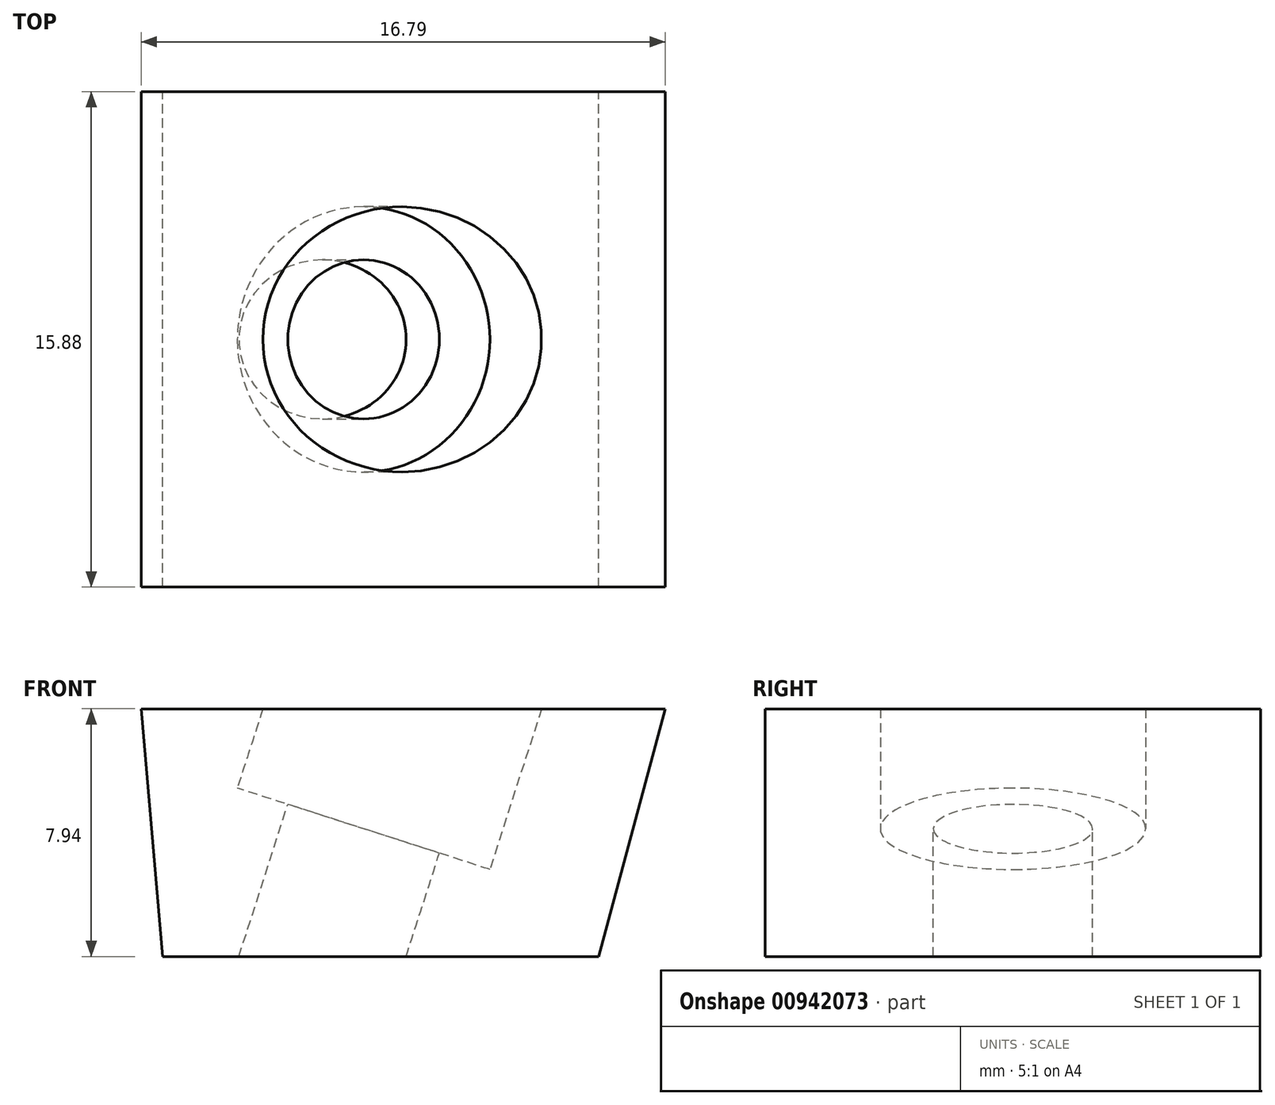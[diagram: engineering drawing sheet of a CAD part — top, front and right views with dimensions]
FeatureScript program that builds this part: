
annotation { "Feature Type Name" : "Feature", "Feature Type Description" : "" }
export const myFeature = defineFeature(function(context is Context, id is Id, definition is map)
    precondition{}
    {
        {
            var Q0;
            Q0=qCreatedBy(makeId("Front.planeOp"),FACE);
            var sketch = newSketch(context, id + "F0", { "sketchPlane" : qUnion([Q0])});
            skLineSegment(sketch, "E0", {"start": v(0, 0) * mm, "end": v(2.13, 7.94) * mm});
            skLineSegment(sketch, "E1", {"start": v(2.13, 7.94) * mm, "end": v(-14.66, 7.94) * mm});
            skLineSegment(sketch, "E2", {"start": v(-14.66, 7.94) * mm, "end": v(-13.97, 0) * mm});
            skLineSegment(sketch, "E3", {"start": v(-13.97, 0) * mm, "end": v(0, 0) * mm});
            skSolve(sketch);
        }
        {
            var Q0;
            Q0=makeQuery(id+"F0.imprint","IMPRINT",FACE,{"disambiguationData":[TD([[makeQuery(id+"F0.imprint","IMPRINT",EDGE,{"derivedFrom":sQuery(id+"F0.wireOp",EDGE,"E0")}),1.0]])]});
            extrude(context, id + "F1", {"entities" : qUnion([Q0]), "depth" : 7.94 * mm, "offsetDistance" : 25.4 * mm, "hasSecondDirection" : true, "secondDirectionOppositeDirection" : true, "secondDirectionDepth" : 7.94 * mm});
        }
        {
            var Q0;
            Q0=qCreatedBy(makeId("Front.planeOp"),FACE);
            var sketch = newSketch(context, id + "F2", { "sketchPlane" : qUnion([Q0])});
            skLineSegment(sketch, "E4", {"start": v(0, 0) * mm, "end": v(-7.98, 2.57) * mm});
            skLineSegment(sketch, "E5", {"start": v(-7.98, 2.57) * mm, "end": v(-1.12, 23.86) * mm});
            skLineSegment(sketch, "E6", {"start": v(-1.12, 23.86) * mm, "end": v(-10.56, -5.44) * mm});
            skSolve(sketch);
        }
        {
            var Q0;
            Q0=sQuery(id+"F2.wireOp",EDGE,"E4");
            cPlane(context, id + "F3", {"entities" : qUnion([Q0]), "cplaneType" : CPlaneType.LINE_ANGLE, "offset" : 25.4 * mm, "angle" : 90 * degree, "width" : 152.4 * mm, "height" : 152.4 * mm});
        }
        {
            var Q0;
            Q0=qCreatedBy(id+"F3.planeOp",FACE);
            var sketch = newSketch(context, id + "F4", { "sketchPlane" : qUnion([Q0])});
            skCircle(sketch, "E7", {"center": v(-8.43, 0) * mm, "radius": 2.55 * mm});
            skCircle(sketch, "E8", {"center": v(-8.43, 0) * mm, "radius": 4.25 * mm});
            skSolve(sketch);
        }
        {
            var Q0;
            Q0=makeQuery(id+"F4.imprint","IMPRINT",FACE,{"disambiguationData":[TD([[makeQuery(id+"F4.imprint","IMPRINT",EDGE,{"derivedFrom":sQuery(id+"F4.wireOp",EDGE,"E7")}),1.0]])]});
            extrude(context, id + "F5", {"entities" : qUnion([Q0]), "operationType" : NewBodyOperationType.REMOVE, "oppositeDirection" : true, "depth" : 25.4 * mm, "offsetDistance" : 25.4 * mm, "hasSecondDirection" : true, "secondDirectionOppositeDirection" : false, "secondDirectionDepth" : 25.4 * mm});
        }
        {
            var Q0;
            Q0=makeQuery(id+"F4.imprint","IMPRINT",FACE,{"disambiguationData":[TD([[makeQuery(id+"F4.imprint","IMPRINT",EDGE,{"derivedFrom":sQuery(id+"F4.wireOp",EDGE,"E7")}),-1.0]])]});
            extrude(context, id + "F6", {"entities" : qUnion([Q0]), "operationType" : NewBodyOperationType.REMOVE, "depth" : 25.4 * mm, "offsetDistance" : 25.4 * mm, "hasSecondDirection" : true, "secondDirectionOppositeDirection" : false, "secondDirectionDepth" : 1.59 * mm});
        }
    });
